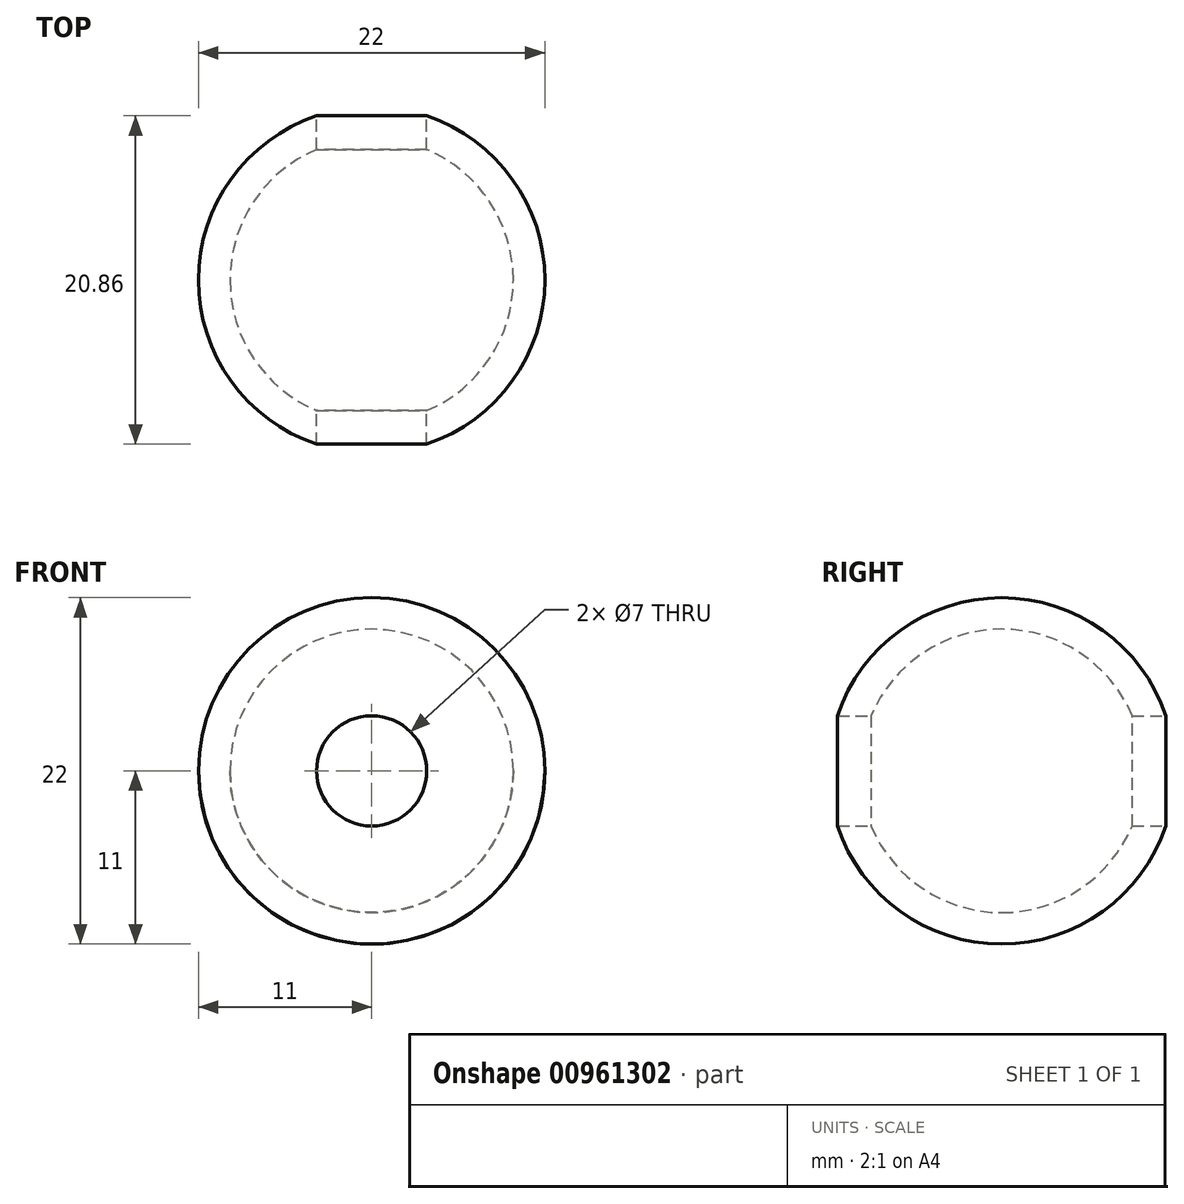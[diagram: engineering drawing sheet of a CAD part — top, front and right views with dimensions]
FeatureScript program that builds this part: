
annotation { "Feature Type Name" : "Feature", "Feature Type Description" : "" }
export const myFeature = defineFeature(function(context is Context, id is Id, definition is map)
    precondition{}
    {
        {
            var Q0;
            Q0=qCreatedBy(makeId("Top.planeOp"),FACE);
            var sketch = newSketch(context, id + "F0", { "sketchPlane" : qUnion([Q0])});
            skArc(sketch, "E0", {"start": v(-11, 0) * mm, "mid": v(0, -11) * mm, "end": v(11, 0) * mm});
            skLineSegment(sketch, "E1", {"start": v(-11, 0) * mm, "end": v(18.18, 0) * mm});
            skSolve(sketch);
        }
        {
            var Q0;
            Q0 = qSketchRegion(id + "F0", true);
            var Q1;
            Q1=sQuery(id+"F0.wireOp",EDGE,"E1");
            revolve(context, id + "F1", {"surfaceOperationType" : NewSurfaceOperationType.NEW, "entities" : qUnion([Q0]), "axis" : qUnion([Q1]), "revolveType" : RevolveType.FULL});
        }
        {
            var Q0;
            Q0=qCreatedBy(makeId("Front.planeOp"),FACE);
            var sketch = newSketch(context, id + "F2", { "sketchPlane" : qUnion([Q0])});
            skCircle(sketch, "E2", {"center": v(0, 0) * mm, "radius": 3.5 * mm});
            skSolve(sketch);
        }
        {
            var Q0;
            Q0 = qSketchRegion(id + "F2", true);
            extrude(context, id + "F3", {"entities" : qUnion([Q0]), "operationType" : NewBodyOperationType.REMOVE, "endBound" : BoundingType.SYMMETRIC, "depth" : 25 * mm, "offsetDistance" : 25 * mm});
        }
        {
            var Q0;
            Q0=makeQuery(id+"F3.boolean.opBoolean","COPY",FACE,{"derivedFrom":makeQuery(id+"F3.opExtrude","SWEPT_FACE",FACE,{"disambiguationData":[OSD([sQuery(id+"F2.wireOp",EDGE,"E2")])]})});
            shell(context, id + "F4", {"entities" : qUnion([Q0]), "thickness" : 2 * mm});
        }
        {
            var Q0;
            Q0=qCreatedBy(makeId("Front.planeOp"),FACE);
            var sketch = newSketch(context, id + "F5", { "sketchPlane" : qUnion([Q0])});
            skLineSegment(sketch, "E3", {"start": v(0, 0) * mm, "end": v(22.74, 0) * mm});
            skSolve(sketch);
        }
        {
            var Q0;
            Q0=qCreatedBy(makeId("Right.planeOp"),FACE);
            var sketch = newSketch(context, id + "F6", { "sketchPlane" : qUnion([Q0])});
            skArc(sketch, "E4", {"start": v(2.18, 10.78) * mm, "mid": v(-5.5, -9.53) * mm, "end": v(8.25, 7.28) * mm});
            skLineSegment(sketch, "E5", {"start": v(8.25, 7.28) * mm, "end": v(2.18, 10.78) * mm});
            skLineSegment(sketch, "E6", {"start": v(0, 0) * mm, "end": v(5.21, 9.03) * mm});
            skLineSegment(sketch, "E7.0", {"start": v(-2.18, 10.78) * mm, "end": v(-8.25, 7.28) * mm});
            skLineSegment(sketch, "E8.0", {"start": v(-10.43, 3.5) * mm, "end": v(-10.43, -3.5) * mm});
            skSolve(sketch);
        }
    });
